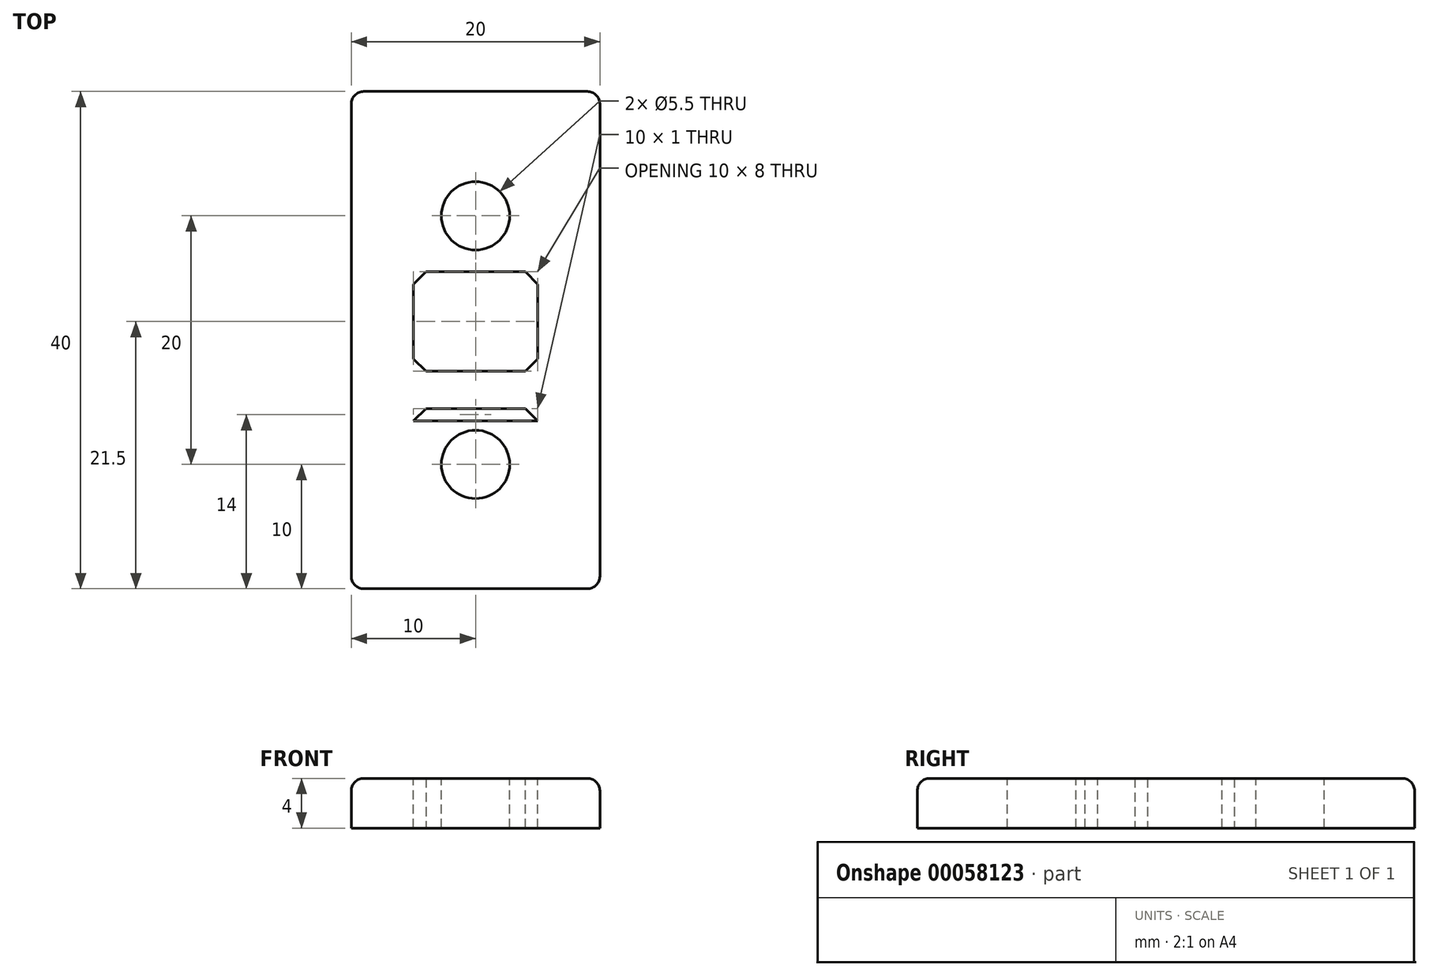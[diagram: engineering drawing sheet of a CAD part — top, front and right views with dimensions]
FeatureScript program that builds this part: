
annotation { "Feature Type Name" : "Feature", "Feature Type Description" : "" }
export const myFeature = defineFeature(function(context is Context, id is Id, definition is map)
    precondition{}
    {
        {
            var Q0;
            Q0=qCreatedBy(makeId("Top.planeOp"),FACE);
            var sketch = newSketch(context, id + "F5", { "sketchPlane" : qUnion([Q0])});
            skLineSegment(sketch, "E0.rect.bottom", {"start": v(10, -20) * mm, "end": v(-10, -20) * mm});
            skLineSegment(sketch, "E0.rect.top", {"start": v(10, 20) * mm, "end": v(-10, 20) * mm});
            skLineSegment(sketch, "E0.rect.left", {"start": v(10, -20) * mm, "end": v(10, 20) * mm});
            skLineSegment(sketch, "E0.rect.right", {"start": v(-10, -20) * mm, "end": v(-10, 20) * mm});
            skPoint(sketch, "E0.rect.middle", {"position": v(0, 0) * mm});
            skSolve(sketch);
        }
        {
            var Q0;
            Q0=makeQuery(id+"F5.imprint","IMPRINT",FACE,{"disambiguationData":[TD([[makeQuery(id+"F5.imprint","IMPRINT",EDGE,{"derivedFrom":sQuery(id+"F5.wireOp",EDGE,"E0.rect.bottom")}),-1.0]])]});
            extrude(context, id + "F6", {"entities" : qUnion([Q0]), "depth" : 4 * mm});
        }
        {
            var Q0;
            Q0=makeQuery(id+"F6.opExtrude","CAP_FACE",FACE,{"disambiguationData":[OSD([sQuery(id+"F5.wireOp",EDGE,"E0.rect.bottom"),sQuery(id+"F5.wireOp",EDGE,"E0.rect.top"),sQuery(id+"F5.wireOp",EDGE,"E0.rect.left"),sQuery(id+"F5.wireOp",EDGE,"E0.rect.right")])],"isStart":false});
            var sketch = newSketch(context, id + "F0", { "sketchPlane" : qUnion([Q0])});
            skPoint(sketch, "E1", {"position": v(0, 10) * mm});
            skPoint(sketch, "E2", {"position": v(0, -10) * mm});
            skSolve(sketch);
        }
        {
            var Q0;
            Q0=sQuery(id+"F0.wireOp",VERTEX,"E1");
            var Q1;
            Q1=sQuery(id+"F0.wireOp",VERTEX,"E2");
            var Q2;
            Q2=makeQuery(id+"F6.opExtrude","SWEPT_BODY",BODY,{"disambiguationData":[OSD([sQuery(id+"F5.wireOp",EDGE,"E0.rect.bottom"),sQuery(id+"F5.wireOp",EDGE,"E0.rect.top"),sQuery(id+"F5.wireOp",EDGE,"E0.rect.left"),sQuery(id+"F5.wireOp",EDGE,"E0.rect.right")])]});
            hole(context, id + "F1", {"style" : HoleStyle.SIMPLE, "holeDiameter" : 5.5 * mm, "endStyle" : HoleEndStyle.THROUGH, "locations" : qUnion([Q0, Q1]), "scope" : qUnion([Q2])});
        }
        {
            var Q0;
            Q0=makeQuery(id+"F6.opExtrude","SWEPT_EDGE",EDGE,{"disambiguationData":[OSD([sQuery(id+"F5.wireOp",EDGE,"E0.rect.bottom"),sQuery(id+"F5.wireOp",EDGE,"E0.rect.right")])]});
            var Q1;
            Q1=makeQuery(id+"F6.opExtrude","SWEPT_EDGE",EDGE,{"disambiguationData":[OSD([sQuery(id+"F5.wireOp",EDGE,"E0.rect.bottom"),sQuery(id+"F5.wireOp",EDGE,"E0.rect.left")])]});
            var Q2;
            Q2=makeQuery(id+"F6.opExtrude","SWEPT_EDGE",EDGE,{"disambiguationData":[OSD([sQuery(id+"F5.wireOp",EDGE,"E0.rect.top"),sQuery(id+"F5.wireOp",EDGE,"E0.rect.right")])]});
            var Q3;
            Q3=makeQuery(id+"F6.opExtrude","SWEPT_EDGE",EDGE,{"disambiguationData":[OSD([sQuery(id+"F5.wireOp",EDGE,"E0.rect.top"),sQuery(id+"F5.wireOp",EDGE,"E0.rect.left")])]});
            fillet(context, id + "F2", {"entities" : qUnion([Q0, Q1, Q2, Q3]), "radius" : 1 * mm, "tangentPropagation" : true, "allowEdgeOverflow" : false});
        }
        {
            var Q0;
            Q0=makeQuery(id+"F6.opExtrude","CAP_FACE",FACE,{"disambiguationData":[OSD([sQuery(id+"F5.wireOp",EDGE,"E0.rect.bottom"),sQuery(id+"F5.wireOp",EDGE,"E0.rect.top"),sQuery(id+"F5.wireOp",EDGE,"E0.rect.left"),sQuery(id+"F5.wireOp",EDGE,"E0.rect.right")])],"isStart":false});
            var sketch = newSketch(context, id + "F7", { "sketchPlane" : qUnion([Q0])});
            skLineSegment(sketch, "E3.rect.bottom", {"start": v(5, -6.5) * mm, "end": v(-5, -6.5) * mm});
            skLineSegment(sketch, "E3.rect.left", {"start": v(5, -6.5) * mm, "end": v(5, -5.5) * mm});
            skLineSegment(sketch, "E3.rect.right", {"start": v(-5, -6.5) * mm, "end": v(-5, -5.5) * mm});
            skPoint(sketch, "E3.rect.middle", {"position": v(0, 0) * mm});
            skLineSegment(sketch, "E4.rect.bottom", {"start": v(5, -5.5) * mm, "end": v(-5, -5.5) * mm});
            skLineSegment(sketch, "E4.rect.top", {"start": v(5, 5.5) * mm, "end": v(-5, 5.5) * mm});
            skLineSegment(sketch, "E4.rect.left", {"start": v(5, -2.5) * mm, "end": v(5, 2.5) * mm});
            skLineSegment(sketch, "E4.rect.right", {"start": v(-5, -2.5) * mm, "end": v(-5, 2.5) * mm});
            skLineSegment(sketch, "E5.rect.bottom", {"start": v(5, -2.5) * mm, "end": v(-5, -2.5) * mm});
            skLineSegment(sketch, "E6", {"start": v(5, 5.5) * mm, "end": v(5, -6.5) * mm});
            skLineSegment(sketch, "E7", {"start": v(-5, -6.5) * mm, "end": v(-5, 5.5) * mm});
            skPoint(sketch, "E8.trimOffspring.end.orphan", {"position": v(-5, 6.5) * mm});
            skPoint(sketch, "E9.orphan", {"position": v(5, 6.5) * mm});
            skSolve(sketch);
        }
        {
            var Q0;
            {var subQ0=sQuery(id+"F7.wireOp",EDGE,"E3.rect.top");Q0=makeQuery(id+"F7.imprint","IMPRINT",FACE,{"disambiguationData":[TD([[makeQuery(id+"F7.imprint","IMPRINT",EDGE,{"derivedFrom":subQ0}),1.0]])]});}
            var Q1;
            {var subQ0=sQuery(id+"F7.wireOp",EDGE,"E5.rect.bottom");Q1=makeQuery(id+"F7.imprint","IMPRINT",FACE,{"disambiguationData":[TD([[makeQuery(id+"F7.imprint","IMPRINT",EDGE,{"derivedFrom":subQ0}),-1.0]])]});}
            var Q2;
            {var subQ0=sQuery(id+"F7.wireOp",EDGE,"E4.rect.bottom");Q2=makeQuery(id+"F7.imprint","IMPRINT",FACE,{"disambiguationData":[TD([[makeQuery(id+"F7.imprint","IMPRINT",EDGE,{"derivedFrom":subQ0}),1.0]])]});}
            extrude(context, id + "F8", {"entities" : qUnion([Q0, Q1, Q2]), "operationType" : NewBodyOperationType.REMOVE, "oppositeDirection" : true, "depth" : 25 * mm});
        }
        {
            var Q0;
            Q0=makeQuery(id+"F6.opExtrude","CAP_EDGE",EDGE,{"disambiguationData":[OSD([sQuery(id+"F5.wireOp",EDGE,"E0.rect.bottom")])],"isStart":false});
            var Q1;
            Q1=makeQuery(id+"F6.opExtrude","CAP_EDGE",EDGE,{"disambiguationData":[OSD([sQuery(id+"F5.wireOp",EDGE,"E0.rect.left")])],"isStart":false});
            var Q2;
            Q2=makeQuery(id+"F6.opExtrude","CAP_EDGE",EDGE,{"disambiguationData":[OSD([sQuery(id+"F5.wireOp",EDGE,"E0.rect.top")])],"isStart":false});
            var Q3;
            Q3=makeQuery(id+"F6.opExtrude","CAP_EDGE",EDGE,{"disambiguationData":[OSD([sQuery(id+"F5.wireOp",EDGE,"E0.rect.right")])],"isStart":false});
            fillet(context, id + "F3", {"entities" : qUnion([Q0, Q1, Q2, Q3]), "radius" : 1 * mm, "tangentPropagation" : true, "allowEdgeOverflow" : false});
        }
        {
            var Q0;
            Q0=makeQuery(id+"F8.boolean.opBoolean","COPY",EDGE,{"derivedFrom":makeQuery(id+"F8.opExtrude","SWEPT_EDGE",EDGE,{"disambiguationData":[OSD([sQuery(id+"F7.wireOp",EDGE,"E4.rect.bottom"),sQuery(id+"F7.wireOp",EDGE,"E7")])]})});
            var Q1;
            Q1=makeQuery(id+"F8.boolean.opBoolean","COPY",EDGE,{"derivedFrom":makeQuery(id+"F8.opExtrude","SWEPT_EDGE",EDGE,{"disambiguationData":[OSD([sQuery(id+"F7.wireOp",EDGE,"E4.rect.bottom"),sQuery(id+"F7.wireOp",EDGE,"E6")])]})});
            var Q2;
            Q2=makeQuery(id+"F8.boolean.opBoolean","COPY",EDGE,{"derivedFrom":makeQuery(id+"F8.opExtrude","SWEPT_EDGE",EDGE,{"disambiguationData":[OSD([sQuery(id+"F7.wireOp",EDGE,"E4.rect.top"),sQuery(id+"F7.wireOp",EDGE,"E6")])]})});
            var Q3;
            Q3=makeQuery(id+"F8.boolean.opBoolean","COPY",EDGE,{"derivedFrom":makeQuery(id+"F8.opExtrude","SWEPT_EDGE",EDGE,{"disambiguationData":[OSD([sQuery(id+"F7.wireOp",EDGE,"E4.rect.top"),sQuery(id+"F7.wireOp",EDGE,"E7")])]})});
            var Q4;
            Q4=makeQuery(id+"F8.boolean.opBoolean","COPY",EDGE,{"derivedFrom":makeQuery(id+"F8.opExtrude","SWEPT_EDGE",EDGE,{"disambiguationData":[OSD([sQuery(id+"F7.wireOp",EDGE,"E5.rect.bottom"),sQuery(id+"F7.wireOp",EDGE,"E7")])]})});
            var Q5;
            Q5=makeQuery(id+"F8.boolean.opBoolean","COPY",EDGE,{"derivedFrom":makeQuery(id+"F8.opExtrude","SWEPT_EDGE",EDGE,{"disambiguationData":[OSD([sQuery(id+"F7.wireOp",EDGE,"E5.rect.bottom"),sQuery(id+"F7.wireOp",EDGE,"E6")])]})});
            chamfer(context, id + "F4", {"entities" : qUnion([Q0, Q1, Q2, Q3, Q4, Q5]), "width" : 1 * mm, "tangentPropagation" : true});
        }
    });
